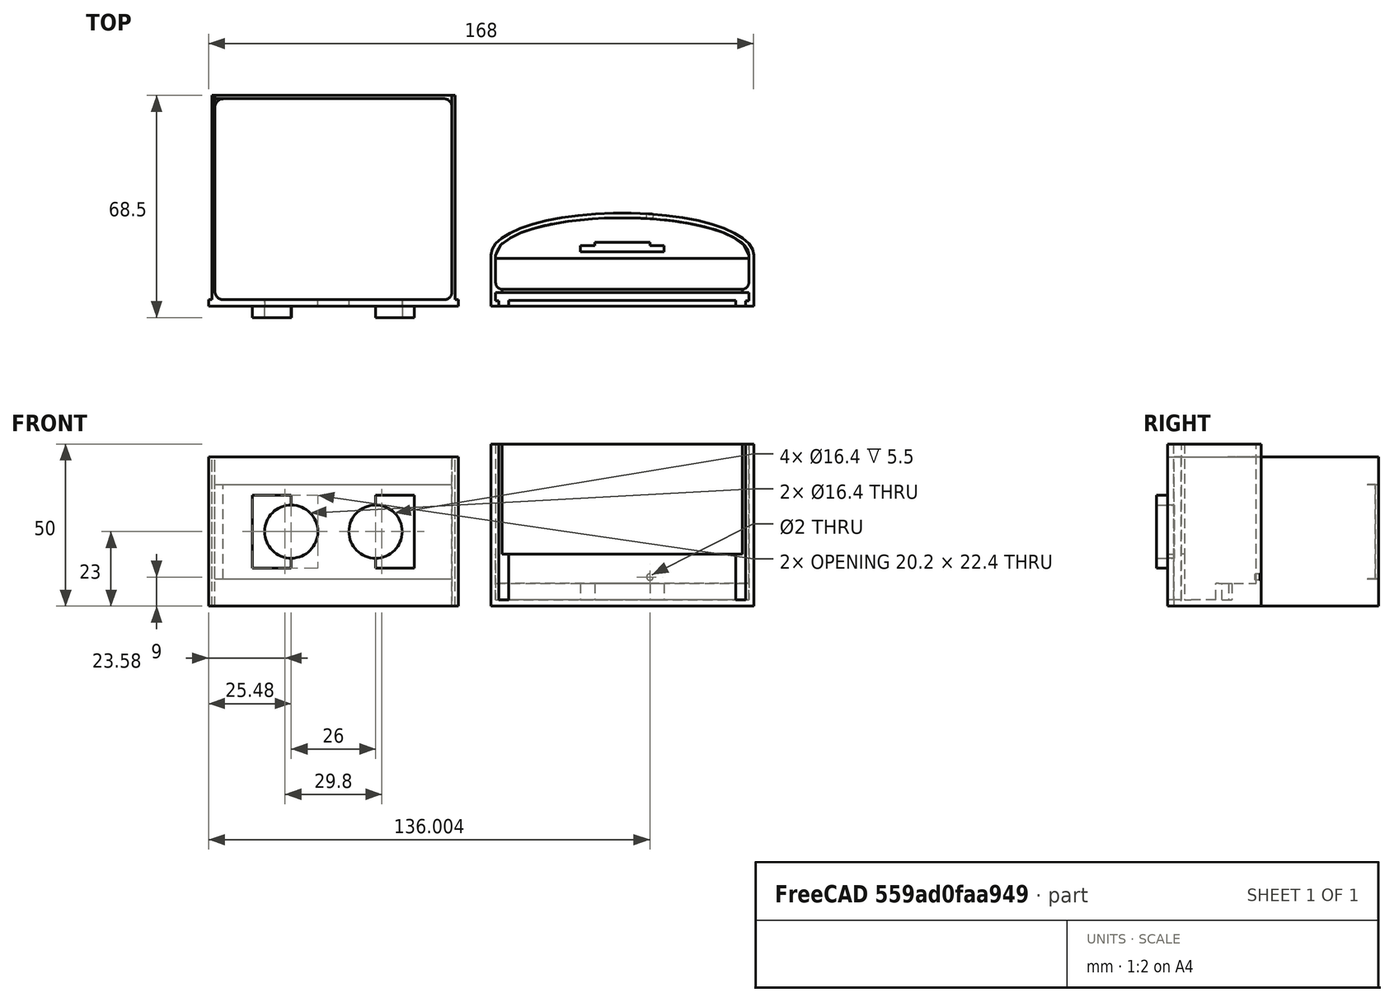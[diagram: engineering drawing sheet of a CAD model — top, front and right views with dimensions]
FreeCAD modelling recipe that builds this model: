
FCSTD DOCUMENT  (FreeCAD 0.18.4R)
Label: sonic.sensor.V2
License: All rights reserved
LicenseURL: http://en.wikipedia.org/wiki/All_rights_reserved
objects: Part::Feature×18, Part::Extrusion×11, Part::MultiFuse×10, Part::FeaturePython×2, App::DocumentObjectGroup×2, Part::Cut×1
note: 42 computed .brp shape members not serialized (recipe doc carries the construction recipe); baked Part::Feature solids carry a one-line shape summary decoded from their .brp

FEATURE [Part::Feature] Face
  shape: bbox 2e-07 x 2 x 46 mm, 1 faces, 0 solids (baked)
FEATURE [Part::Extrusion] Extrusion
  Base = -> Face
  Dir = (12.5236,0,0)
  DirMode = 0
  FaceMakerClass = Part::FaceMakerBullseye
  LengthFwd = 0
  LengthRev = 0
  Solid = true
  Symmetric = false
FEATURE [Part::Feature] Face001
  shape: bbox 2e-07 x 2 x 46 mm, 1 faces, 0 solids (baked)
FEATURE [Part::Extrusion] Extrusion001
  Base = -> Face001
  Dir = (-12.4764,0,0)
  DirMode = 0
  FaceMakerClass = Part::FaceMakerBullseye
  LengthFwd = 0
  LengthRev = 0
  Solid = true
  Symmetric = false
FEATURE [Part::FeaturePython] Slice_child1  label="Slice.1"  # WARN: FeaturePython — macro-defined, semantics opaque (R4)
  FilterType = 1
  Invert = false
  OverrideMaxVal = 0
  WindowFrom = 80
  WindowTo = 100
  items = 1
FEATURE [Part::Feature] Slice_child0002  label="Slice.004"
  Placement = pos=(-25,-4e-15,0) rot=(0,0,1;0rad)
  shape: bbox 36.48 x 63 x 46 mm, 30 faces (baked)
FEATURE [Part::Feature] Face002
  Placement = pos=(-25,-4e-15,0) rot=(0,0,1;0rad)
  shape: bbox 3e-07 x 1 x 29 mm, 1 faces, 0 solids (baked)
FEATURE [Part::Extrusion] Extrusion002
  Base = -> Face002
  Dir = (25,1.11e-13,-1.11e-13)
  DirMode = 0
  FaceMakerClass = Part::FaceMakerBullseye
  LengthFwd = 0
  LengthRev = 0
  Solid = true
  Symmetric = false
FEATURE [Part::MultiFuse] Fusion001
  Shapes = -> [Slice_child0002,Extrusion002]
FEATURE [Part::MultiFuse] Fusion002
  Shapes = -> [Fusion001,Slice_child1]
FEATURE [Part::Feature] Face003
  Placement = pos=(12.5236,0,0) rot=(0,0,1;0rad)
  shape: bbox 2e-07 x 2 x 46 mm, 1 faces, 0 solids (baked)
FEATURE [Part::Extrusion] Extrusion003
  Base = -> Face003
  Dir = (1,0,0)
  DirMode = 0
  FaceMakerClass = Part::FaceMakerBullseye
  LengthFwd = 0
  LengthRev = 0
  Solid = true
  Symmetric = false
FEATURE [Part::Feature] Extrusion004
  Placement = pos=(-76,0,0) rot=(0,0,1;0rad)
  shape: bbox 1 x 2 x 46 mm, 6 faces (baked)
FEATURE [App::DocumentObjectGroup] GrExplode_Slice002  label="Exploded Slice002"
FEATURE [Part::FeaturePython] Slice_child0  label="Slice.0"  # WARN: FeaturePython — macro-defined, semantics opaque (R4)
  FilterType = 1
  Invert = false
  OverrideMaxVal = 0
  WindowFrom = 80
  WindowTo = 100
  items = 0
FEATURE [Part::MultiFuse] Fusion
  Shapes = -> [Slice_child0,Extrusion001,Extrusion]
FEATURE [Part::MultiFuse] Fusion004
  Shapes = -> [Fusion,Extrusion003,Extrusion004,Fusion002]
FEATURE [Part::MultiFuse] Fusion003
  Shapes = -> [Slice_child0,Extrusion001,Extrusion]
FEATURE [Part::MultiFuse] Fusion007
  Shapes = -> [Fusion004,Fusion003]
FEATURE [Part::Feature] Face006
  shape: bbox 4.243e-07 x 3.5 x 3 mm, 1 faces, 0 solids (baked)
FEATURE [Part::Extrusion] Extrusion027
  Base = -> Face006
  Dir = (-1.05678,0,0)
  DirMode = 0
  FaceMakerClass = Part::FaceMakerBullseye
  LengthFwd = 0
  LengthRev = 0
  Solid = true
  Symmetric = false
FEATURE [Part::Feature] Face007
  shape: bbox 2e-07 x 3.5 x 16.4 mm, 1 faces, 0 solids (baked)
FEATURE [Part::Extrusion] Extrusion028
  Base = -> Face007
  Dir = (-1.05678,0,0)
  DirMode = 0
  FaceMakerClass = Part::FaceMakerBullseye
  LengthFwd = 0
  LengthRev = 0
  Solid = true
  Symmetric = false
FEATURE [Part::Feature] Face008
  shape: bbox 4.243e-07 x 3.5 x 3 mm, 1 faces, 0 solids (baked)
FEATURE [Part::Extrusion] Extrusion029
  Base = -> Face008
  Dir = (-1.05678,0,0)
  DirMode = 0
  FaceMakerClass = Part::FaceMakerBullseye
  LengthFwd = 0
  LengthRev = 0
  Solid = true
  Symmetric = false
FEATURE [Part::Feature] Face009
  shape: bbox 4.243e-07 x 3.5 x 3 mm, 1 faces, 0 solids (baked)
FEATURE [Part::Extrusion] Extrusion030
  Base = -> Face009
  Dir = (1,0,0)
  DirMode = 0
  FaceMakerClass = Part::FaceMakerBullseye
  LengthFwd = 0
  LengthRev = 0
  Solid = true
  Symmetric = false
FEATURE [Part::Feature] Face010
  shape: bbox 2e-07 x 3.5 x 16.4 mm, 1 faces, 0 solids (baked)
FEATURE [Part::Extrusion] Extrusion031
  Base = -> Face010
  Dir = (1,0,0)
  DirMode = 0
  FaceMakerClass = Part::FaceMakerBullseye
  LengthFwd = 0
  LengthRev = 0
  Solid = true
  Symmetric = false
FEATURE [Part::Feature] Face011
  shape: bbox 4.243e-07 x 3.5 x 3 mm, 1 faces, 0 solids (baked)
FEATURE [Part::Extrusion] Extrusion032
  Base = -> Face011
  Dir = (1,0,0)
  DirMode = 0
  FaceMakerClass = Part::FaceMakerBullseye
  LengthFwd = 0
  LengthRev = 0
  Solid = true
  Symmetric = false
FEATURE [Part::MultiFuse] Fusion008003008
  Shapes = -> [Extrusion030,Extrusion031,Extrusion032,Fusion007]
FEATURE [Part::MultiFuse] Fusion008003009
  Shapes = -> [Extrusion027,Extrusion028,Fusion008003008]
FEATURE [Part::MultiFuse] Fusion008003010
  Shapes = -> [Fusion008003009,Extrusion029]
FEATURE [App::DocumentObjectGroup] GrExplode_Slice001  label="Exploded Slice001"
  Group = -> [Fusion008003010]
FEATURE [Part::Feature] Fusion008003010001  label="Fusion008003011"
  shape: bbox 77 x 68.5 x 46 mm, 43 faces (baked)
FEATURE [Part::Feature] Face012
  Placement = pos=(-12.4764,-4e-15,0) rot=(0,0,1;0rad)
  shape: bbox 2.5 x 3e-07 x 29 mm, 1 faces, 0 solids (baked)
FEATURE [Part::Extrusion] Extrusion033
  Base = -> Face012
  Dir = (0,0.043591,0)
  DirMode = 0
  FaceMakerClass = Part::FaceMakerBullseye
  LengthFwd = 0
  LengthRev = 0
  Solid = true
  Symmetric = false
FEATURE [Part::MultiFuse] Fusion008003010002
  Shapes = -> [Fusion008003010001,Extrusion033]
FEATURE [Part::Feature] Fusion008003010002001  label="Fusion008003010003"
  shape: bbox 77 x 68.5 x 46 mm, 41 faces (baked)
FEATURE [Part::Feature] Extrusion034
  Placement = pos=(-61.0926,4.24998,-1.7e-14) rot=(0,0,1;0rad)
  shape: bbox 2 x 19 x 2 mm, 3 faces (baked)
FEATURE [Part::Feature] Fusion008003010002002  label="Fusion008003010004"
  Placement = pos=(-61.0926,4.24998,-1.7e-14) rot=(0,0,1;0rad)
  shape: bbox 81 x 28.75 x 50 mm, 53 faces (baked)
FEATURE [Part::Feature] Face013
  Placement = pos=(-61.0926,4.24998,-1.7e-14) rot=(0,0,1;0rad)
  shape: bbox 78 x 12.5 x 1e-05 mm, 1 faces, 0 solids (baked)
FEATURE [Part::Cut] Cut
  Base = -> Fusion008003010002002
  Tool = -> Extrusion034
